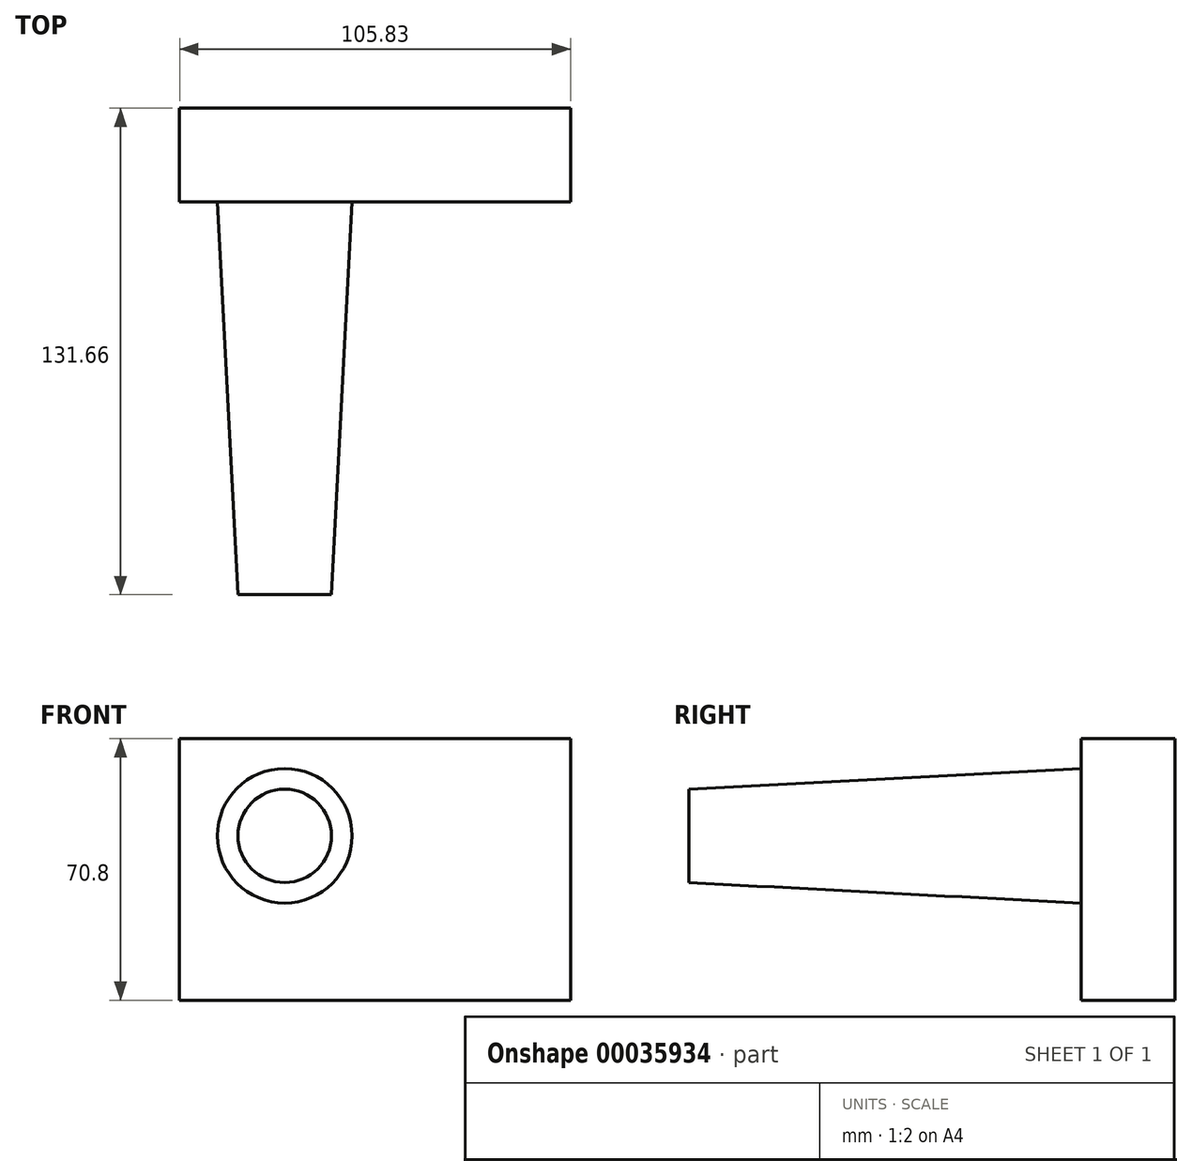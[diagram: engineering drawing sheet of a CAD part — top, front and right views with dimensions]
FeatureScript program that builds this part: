
annotation { "Feature Type Name" : "Feature", "Feature Type Description" : "" }
export const myFeature = defineFeature(function(context is Context, id is Id, definition is map)
    precondition{}
    {
        {
            var Q0;
            Q0=qCreatedBy(makeId("Front.planeOp"),FACE);
            var sketch = newSketch(context, id + "F0", { "sketchPlane" : qUnion([Q0])});
            skLineSegment(sketch, "E0.bottom", {"start": v(-68.6, 54.78) * mm, "end": v(37.24, 54.78) * mm});
            skLineSegment(sketch, "E0.top", {"start": v(-68.6, -16.02) * mm, "end": v(37.24, -16.02) * mm});
            skLineSegment(sketch, "E0.left", {"start": v(-68.6, 54.78) * mm, "end": v(-68.6, -16.02) * mm});
            skLineSegment(sketch, "E0.right", {"start": v(37.24, 54.78) * mm, "end": v(37.24, -16.02) * mm});
            skSolve(sketch);
        }
        {
            var Q0;
            Q0 = qSketchRegion(id + "F0", true);
            extrude(context, id + "F1", {"entities" : qUnion([Q0]), "depth" : 25.4 * mm});
        }
        {
            var Q0;
            Q0=makeQuery(id+"F1.opExtrude","CAP_FACE",FACE,{"disambiguationData":[OSD([sQuery(id+"F0.wireOp",EDGE,"E0.bottom"),sQuery(id+"F0.wireOp",EDGE,"E0.top"),sQuery(id+"F0.wireOp",EDGE,"E0.left"),sQuery(id+"F0.wireOp",EDGE,"E0.right")])],"isStart":false});
            var sketch = newSketch(context, id + "F2", { "sketchPlane" : qUnion([Q0])});
            skCircle(sketch, "E1", {"center": v(-40.14, 28.47) * mm, "radius": 18.22 * mm});
            skSolve(sketch);
        }
        {
            var Q0;
            Q0 = qSketchRegion(id + "F2", true);
            extrude(context, id + "F3", {"entities" : qUnion([Q0]), "operationType" : NewBodyOperationType.ADD, "depth" : 106.26 * mm, "hasDraft" : true, "draftAngle" : 3 * degree, "draftPullDirection" : true});
        }
        {
            var Q0;
            Q0=makeQuery(id+"F1.opExtrude","SWEPT_FACE",FACE,{"disambiguationData":[OSD([sQuery(id+"F0.wireOp",EDGE,"E0.bottom")])]});
            var sketch = newSketch(context, id + "F4", { "sketchPlane" : qUnion([Q0])});
            skCircle(sketch, "E2", {"center": v(-46.83, -10.63) * mm, "radius": 7.85 * mm});
            skSolve(sketch);
        }
        {
            var Q0;
            Q0=sQuery(id+"F4.wireOp",EDGE,"E2");
            extrude(context, id + "F5", {"bodyType" : ToolBodyType.SURFACE, "surfaceEntities" : qUnion([Q0]), "depth" : 25.4 * mm});
        }
    });
